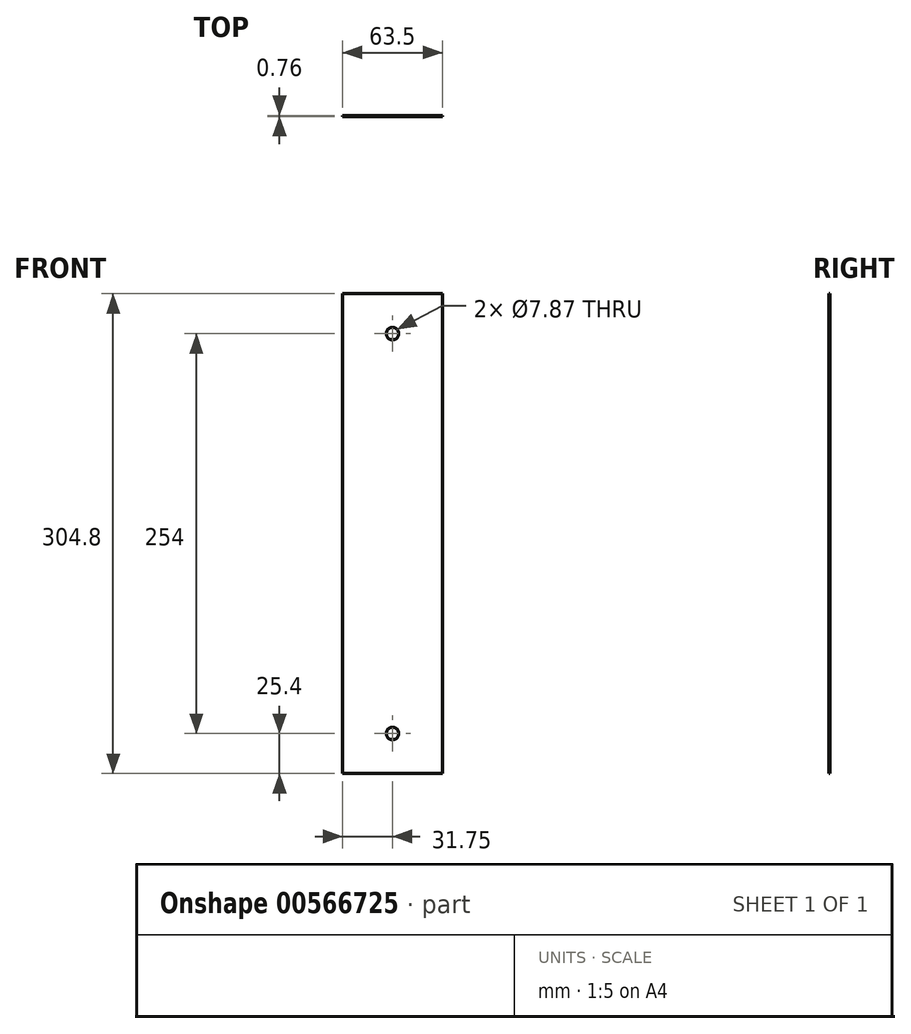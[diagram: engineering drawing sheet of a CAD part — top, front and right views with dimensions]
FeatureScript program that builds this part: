
annotation { "Feature Type Name" : "Feature", "Feature Type Description" : "" }
export const myFeature = defineFeature(function(context is Context, id is Id, definition is map)
    precondition{}
    {
        {
            var Q0;
            Q0=qCreatedBy(makeId("Front.planeOp"),FACE);
            var sketch = newSketch(context, id + "F0", { "sketchPlane" : qUnion([Q0])});
            skLineSegment(sketch, "E0.bottom", {"start": v(31.75, -152.4) * mm, "end": v(-31.75, -152.4) * mm});
            skLineSegment(sketch, "E0.top", {"start": v(31.75, 152.4) * mm, "end": v(-31.75, 152.4) * mm});
            skLineSegment(sketch, "E0.left", {"start": v(31.75, -152.4) * mm, "end": v(31.75, 152.4) * mm});
            skLineSegment(sketch, "E0.right", {"start": v(-31.75, -152.4) * mm, "end": v(-31.75, 152.4) * mm});
            skPoint(sketch, "E0.middle", {"position": v(0, 0) * mm});
            skSolve(sketch);
        }
        {
            var Q0;
            Q0=qSketchRegion(id+"F0",true);
            extrude(context, id + "F1", {"entities" : qUnion([Q0]), "depth" : 0.76 * mm, "offsetDistance" : 25.4 * mm});
        }
        {
            var Q0;
            Q0=qCreatedBy(makeId("Front.planeOp"),FACE);
            var sketch = newSketch(context, id + "F2", { "sketchPlane" : qUnion([Q0])});
            skPoint(sketch, "E1", {"position": v(0, 127) * mm});
            skCircle(sketch, "E2", {"center": v(0, 127) * mm, "radius": 3.94 * mm});
            skPoint(sketch, "E3", {"position": v(0, -127) * mm});
            skCircle(sketch, "E4", {"center": v(0, -127) * mm, "radius": 3.94 * mm});
            skSolve(sketch);
        }
        {
            var Q0;
            Q0=qSketchRegion(id+"F2",true);
            extrude(context, id + "F3", {"entities" : qUnion([Q0]), "operationType" : NewBodyOperationType.REMOVE, "endBound" : BoundingType.SYMMETRIC, "depth" : 25.4 * mm, "offsetDistance" : 25.4 * mm});
        }
    });
